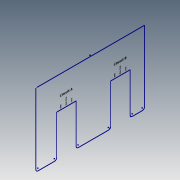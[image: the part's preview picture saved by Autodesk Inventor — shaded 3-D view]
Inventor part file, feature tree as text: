
AUTODESK INVENTOR PART (.ipt)
format: ipt  version: 2020.5 (Build 245400000, 400)  size: 138,240 bytes
history: native  units: mm
features: sketch x1
ambient origin geometry x8: Origin, YZ Plane, XZ Plane, XY Plane, X Axis, Y Axis, Z Axis, Center Point
feature tree (1):
  sketch  "Sketch30"  dims[d13=18.0mm d14=60.0mm d660=11.8mm d661=2.1mm d662=7.08mm d663=1.33mm d664=3.18mm d665=1.05mm d666=1.05mm d667=3.3mm d668=11.8mm d669=2.1mm d670=7.08mm d671=1.33mm d672=3.18mm d673=1.05mm d674=1.05mm d675=3.3mm d676=17.6mm d677=27.899893mm d678=25.82mm d679=21.92mm d680=25.7mm d681=27.604893mm d682=22.664893mm d683=17.444893mm d684=22.100107mm d685=17.6mm d686=22.395107mm d687=25.82mm d688=21.92mm d689=27.335107mm d690=25.7mm d691=32.555107mm]
